# Revit family: Facade_60_Curtain_Wall_I21_Standard
name_source: partatom
category: Windows
revit_build: Autodesk Revit 2014 (Build: 20130308_1515(x64)
units: mm (PartAtom-declared; Revit-internal decimal feet)

## types (23) — shared parameters
Custom Curtain Wall Height = 4990 mm  [stored 16.3714 ft]
DG Gasket Thickness = 12 mm  [stored 0.0393701 ft]
Description = Curtain Wall, I21
Frame Bottom Gap = 30 mm  [stored 0.0984252 ft]
Frame Thickness = 102 mm
Glazing Bottom Gap = 70 mm
Glazing Side Gap = 40 mm  [stored 0.131234 ft]
Glazing Top Gap = 40 mm  [stored 0.131234 ft]
Half Expansion Break = No
Jamb Width = 60 mm  [stored 0.19685 ft]
Limit Door Height Max = 6110 mm
Limit Door Height Min = 410 mm
Limit Door Width Max = 6099 mm
Limit Door Width Min = 699 mm
Limit Panel Height Max = 6000 mm  [stored 19.685 ft]
Limit Panel Height Min = 300 mm
Limit Panel Width Max = 3000 mm  [stored 9.84252 ft]
Limit Panel Width Min = 300 mm
Manufacturer = Crealco
Max System DG Unit Thickness = 25 mm  [stored 0.082021 ft]
Model = Facade 60
Quarter Expansion Break = No
Sill Height = 85 mm  [stored 0.278871 ft]
Thermal Break Material = Plastic, Opaque Black
Top Profile Overhang = 6 mm  [stored 0.019685 ft]
URL = http://www.crealco.co.za
Wall Closure = By host
zero-valued in all types: Custom Anchor Height, Default Sill Height

## per-type parameters (varying)
| type | Custom Curtain Wall Width | Custom Windload | Intruderprufe Insulated LowE SHGC Value | Intruderprufe Insulated LowE U Value | Intruderprufe Insulated SHGC Value | Intruderprufe Insulated U Value | Intruderprufe LowE SHGC Value | Intruderprufe LowE U Value | Intruderprufe SHGC Value | Intruderprufe U Value |
| F60-I21-1850-1000Pa | 1790 mm  [stored 5.8727 ft] | 1000 mm  [stored 3.28084 ft] | 0.557 | 2.33 | 0.618 | 3 | 0.629 | 4.04 | 0.718 | 5.62 |
| F60-I21-1850-1500Pa | 1790 mm  [stored 5.8727 ft] | 1500 mm  [stored 4.92126 ft] | 0.557 | 2.33 | 0.618 | 3 | 0.629 | 4.04 | 0.718 | 5.62 |
| F60-I21-1850-2000Pa | 1790 mm  [stored 5.8727 ft] | 2000 mm  [stored 6.56168 ft] | 0.557 | 2.33 | 0.618 | 3 | 0.629 | 4.04 | 0.718 | 5.62 |
| F60-I21-2450-1000Pa | 2390 mm  [stored 7.84121 ft] | 1000 mm  [stored 3.28084 ft] | 0.563 | 2.29 | 0.625 | 2.97 | 0.636 | 4 | 0.726 | 5.64 |
| F60-I21-2450-1500Pa | 2390 mm  [stored 7.84121 ft] | 1500 mm  [stored 4.92126 ft] | 0.563 | 2.29 | 0.625 | 2.97 | 0.636 | 4 | 0.726 | 5.64 |
| F60-I21-2450-2000Pa | 2390 mm  [stored 7.84121 ft] | 2000 mm  [stored 6.56168 ft] | 0.563 | 2.29 | 0.625 | 2.97 | 0.636 | 4 | 0.726 | 5.64 |
| F60-I21-3050-1000Pa | 2990 mm | 1000 mm  [stored 3.28084 ft] | 0.571 | 2.24 | 0.634 | 2.93 | 0.646 | 3.96 | 0.738 | 5.66 |
| F60-I21-3050-1500Pa | 2990 mm | 1500 mm  [stored 4.92126 ft] | 0.571 | 2.24 | 0.634 | 2.93 | 0.646 | 3.96 | 0.738 | 5.66 |
| F60-I21-3050-2000Pa | 2990 mm | 2000 mm  [stored 6.56168 ft] | 0.571 | 2.24 | 0.634 | 2.93 | 0.646 | 3.96 | 0.738 | 5.66 |
| F60-I21-3650-1000Pa | 3590 mm | 1000 mm  [stored 3.28084 ft] | 0.577 | 2.2 | 0.64 | 2.91 | 0.652 | 3.92 | 0.745 | 5.68 |
| F60-I21-3650-1500Pa | 3590 mm | 1500 mm  [stored 4.92126 ft] | 0.577 | 2.2 | 0.64 | 2.91 | 0.652 | 3.92 | 0.745 | 5.68 |
| F60-I21-4250-2000Pa | 4190 mm  [stored 13.7467 ft] | 2000 mm  [stored 6.56168 ft] | 0.581 | 2.18 | 0.645 | 2.89 | 0.657 | 3.9 | 0.751 | 5.69 |
| F60-I21-4250-1500Pa | 4190 mm  [stored 13.7467 ft] | 1500 mm  [stored 4.92126 ft] | 0.581 | 2.18 | 0.645 | 2.89 | 0.657 | 3.9 | 0.751 | 5.69 |
| F60-I21-4250-1000Pa | 4190 mm  [stored 13.7467 ft] | 1000 mm  [stored 3.28084 ft] | 0.581 | 2.18 | 0.645 | 2.89 | 0.657 | 3.9 | 0.751 | 5.69 |
| F60-I21-4850-1000Pa | 4790 mm  [stored 15.7152 ft] | 1000 mm  [stored 3.28084 ft] | 0.584 | 2.16 | 0.648 | 2.88 | 0.661 | 3.88 | 0.755 | 5.7 |
| F60-I21-4850-1500Pa | 4790 mm  [stored 15.7152 ft] | 1500 mm  [stored 4.92126 ft] | 0.584 | 2.16 | 0.648 | 2.88 | 0.661 | 3.88 | 0.755 | 5.7 |
| F60-I21-4850-2000Pa | 4790 mm  [stored 15.7152 ft] | 2000 mm  [stored 6.56168 ft] | 0.584 | 2.16 | 0.648 | 2.88 | 0.661 | 3.88 | 0.755 | 5.7 |
| F60-I21-5450-1000Pa | 5390 mm  [stored 17.6837 ft] | 1000 mm  [stored 3.28084 ft] | 0.586 | 2.14 | 0.651 | 2.87 | 0.663 | 3.87 | 0.758 | 5.71 |
| F60-I21-5450-1500Pa | 5390 mm  [stored 17.6837 ft] | 1500 mm  [stored 4.92126 ft] | 0.586 | 2.14 | 0.651 | 2.87 | 0.663 | 3.87 | 0.758 | 5.71 |
| F60-I21-5450-2000Pa | 5390 mm  [stored 17.6837 ft] | 2000 mm  [stored 6.56168 ft] | 0.586 | 2.14 | 0.651 | 2.87 | 0.663 | 3.87 | 0.758 | 5.71 |
| F60-I21-6050-1000Pa | 5990 mm  [stored 19.6522 ft] | 1000 mm  [stored 3.28084 ft] | 0.588 | 2.13 | 0.653 | 2.86 | 0.665 | 3.86 | 0.76 | 5.71 |
| F60-I21-6050-1500Pa | 5990 mm  [stored 19.6522 ft] | 1500 mm  [stored 4.92126 ft] | 0.588 | 2.13 | 0.653 | 2.86 | 0.665 | 3.86 | 0.76 | 5.71 |
| F60-I21-6050-2000Pa | 5990 mm  [stored 19.6522 ft] | 2000 mm  [stored 6.56168 ft] | 0.588 | 2.13 | 0.653 | 2.86 | 0.665 | 3.86 | 0.76 | 5.71 |

note: [stored X ft] marks values corroborated as IEEE doubles in the binary element streams (Revit-internal decimal feet)

## geometry (parser evidence)
native form markers: Sweep x16
no freeform markers — native parametric forms only
